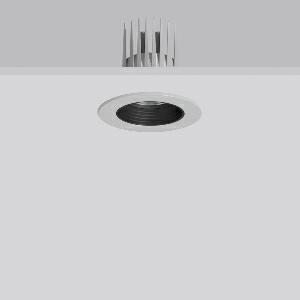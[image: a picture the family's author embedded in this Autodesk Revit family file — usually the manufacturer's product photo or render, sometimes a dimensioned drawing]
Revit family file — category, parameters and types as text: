
# Revit family: heledon_mini_e_901751_004_2_0558
name_source: partatom
category: Lighting Fixtures
units: mm (PartAtom-declared; Revit-internal decimal feet)

## family parameters
Cut with Voids When Loaded = No
Host = Face
Light Source = No
Part Type = Normal
Room Calculation Point = No
Round Connector Dimension = Use Diameter
Shared = No

## types (1)
- HELEDON mini E (1 x LED Modul 927, 3000 lm, 2700)
    Apparent Load = 29 VA
    Approval mark = CE
    CIE Flux Codes = 99 100 100 100 100
    Color Rendering = 92
    Color Temperature = 2700
    Default Elevation = 1800 mm
    Description = Series: HELEDON mini
Round recessed downlight. Housing: die-cast aluminium, powder-coated. Black plastic ring and recessed LED to prevent glare from the side. Optical assembly with lens made of plastic (polycarbonate) for the best homogeneous light distribution - can be changed without tools. Best colour rendering index Ra>90. Suitable for Recessed ceiling mounting. Installation without tools thanks to spring fastening system. Including separate LED converter with connecting cable 600 mm.High quality converter without flickering and stroboscopic effect. Through-wiring box (5 pole) available as accessory. The following accessories can be mounted without use of tools: interchangeable lenses, decorative glasses, honeycomb louvre, clear and frosted diffusers, white interchangeable plastic ring. 
Colour: silver
Diameter: 124 mm
Height: 3 mm
Cut-out diameter: 114 mm
Recess height: 170 mm
Luminaire: recess height: 120 mm
Lamp: LED
Socket: without socket
Colour temperature: 2700K
Colour rendering index (CRI): 92
System power: 29 W
Rated luminous flux: 3000 lm
Luminous efficiency: 103 lm/W
Control gear: Regulated power supply
Protection class: II
Type of protection: IP 20
    Height = 0 mm  [stored 0 ft]
    Lamp = 1 x LED Modul 927
    Lamp Light Flux = 3000 lm
    Lamp count = 1
    Length = 124 mm  [stored 0.406824 ft]
    Lifetime = 50000 h
    Luminous efficacy = 103 lm/W
    Manufacturer = RZB
    ModVariant = No
    Model = 901751.004.2
    Mounting Place = Ceiling
    Mounting Type = Recessed
    Number of Poles = 1
    OnlyDefault = Yes
    Power Factor = 1
    Product Name = HELEDON mini E
    Product group = Recessed downlights
    ProductGroupID = 402
    Protection Class = Protection class II
    Protection Degree = IP 20
    RLX_Detail_Level = 1
    RLX_Emergency_Light_Flux = 0 lm
    RLX_Emergency_Type = 0
    RLX_Emergency_Type_DB = No
    RlxData = <blob elided: 128033 chars, md5=9c2f45ac>
    Socket = socket
    Standby Power = 0 W
    System Light Flux = 3000 lm
    System Power = 29 W
    Type Comments = Product without accessories
    Type Image = 901656.004.jpg
    URL = http://relux.com
    VarID = ---
    Voltage = 230 V
    Voltage Range = 220-240 V
    Weight = 0.00 kg
    Width = 0 mm  [stored 0 ft]

note: [stored X ft] marks values corroborated as IEEE doubles in the binary element streams (Revit-internal decimal feet)

## geometry (parser evidence)
native form markers: Blend x4, Sweep x10
no freeform markers — native parametric forms only
